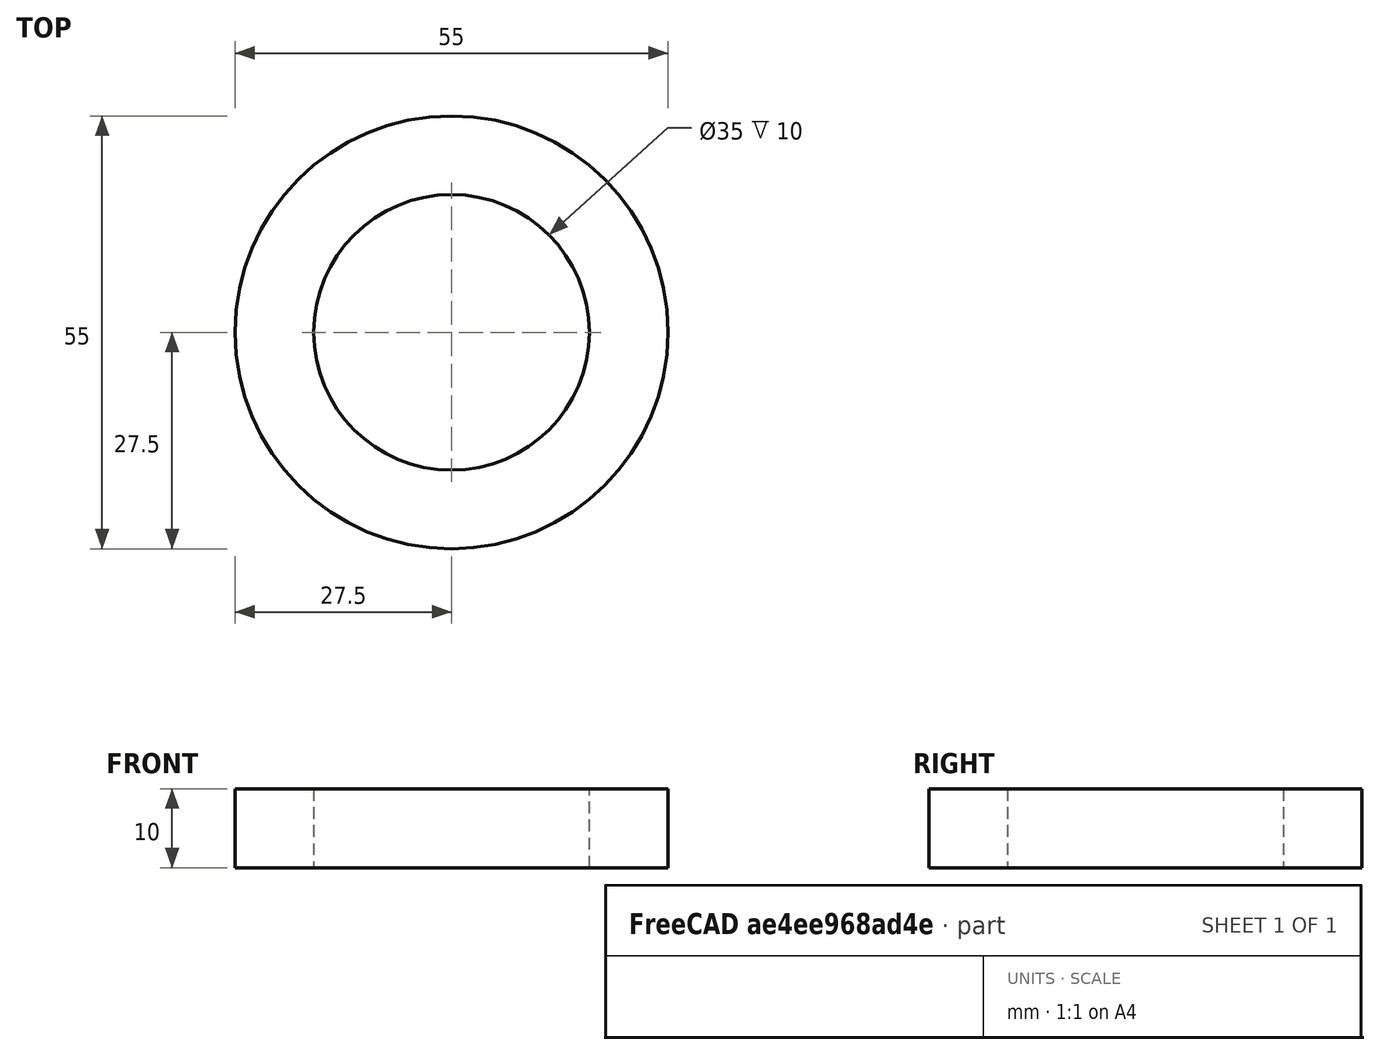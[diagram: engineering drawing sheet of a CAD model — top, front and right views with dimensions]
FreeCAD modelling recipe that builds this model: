
FCSTD DOCUMENT  (FreeCAD 0.19R24276 (Git))
Label: podshipnik_55x35
License: All rights reserved
LicenseURL: http://en.wikipedia.org/wiki/All_rights_reserved
objects: Sketcher::SketchObject×1, PartDesign::Pad×1, PartDesign::Body×1
note: 4 computed .brp shape members not serialized (recipe doc carries the construction recipe); baked Part::Feature solids carry a one-line shape summary decoded from their .brp

FEATURE [Sketcher::SketchObject] Sketch
  FullyConstrained = true
  MapMode = 5
  Support = -> [XY_Plane]
  sketch-geometry (2):
    g0: Circle CenterX=0 CenterY=0 CenterZ=0 NormalX=0 NormalY=0 NormalZ=1 AngleXU=0 Radius=17.5
    g1: Circle CenterX=0 CenterY=0 CenterZ=0 NormalX=0 NormalY=0 NormalZ=1 AngleXU=0 Radius=27.5
  constraints (4):
    c: Coincident(g-1,g0)
    c: Diameter(g0) = 35
    c: Coincident(g0,g1)
    c: Diameter(g1) = 55
FEATURE [PartDesign::Pad] Pad
  Direction = (1,1,1)
  Length = 10
  Length2 = 100
  Profile = -> Sketch
  Type = 0
FEATURE [PartDesign::Body] Body
  Group = -> [Sketch,Pad]
  Origin = -> Origin
  Tip = -> Pad
